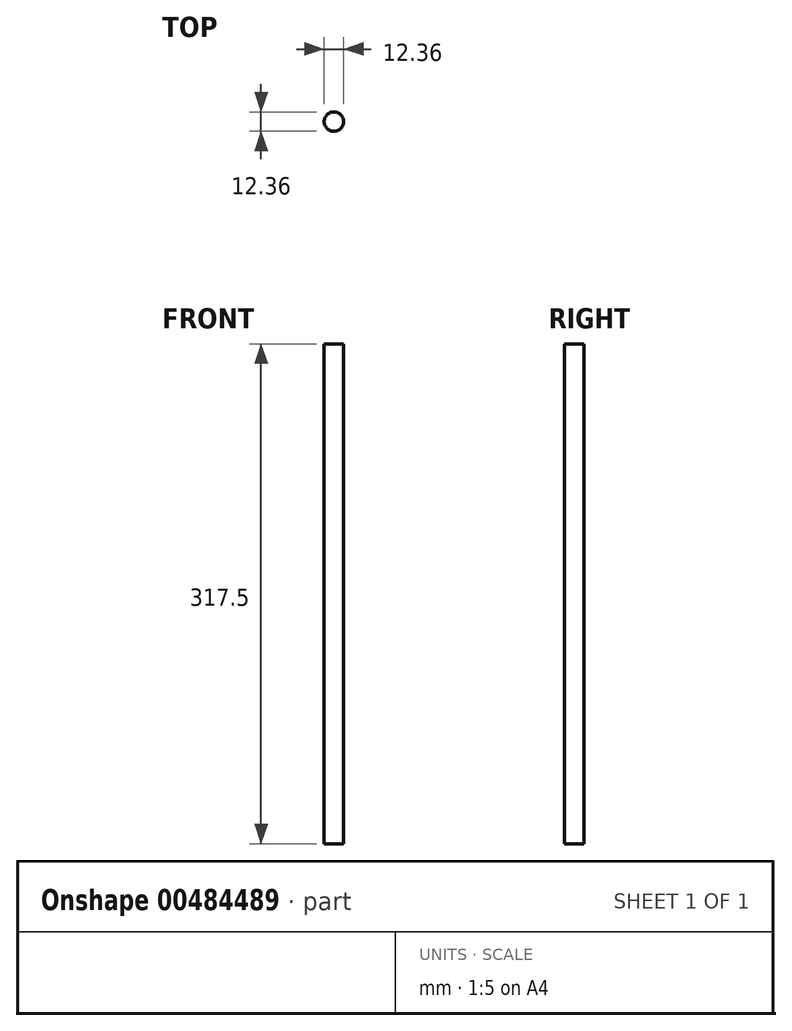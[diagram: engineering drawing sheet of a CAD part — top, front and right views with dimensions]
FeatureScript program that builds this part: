
annotation { "Feature Type Name" : "Feature", "Feature Type Description" : "" }
export const myFeature = defineFeature(function(context is Context, id is Id, definition is map)
    precondition{}
    {
        {
            var Q0;
            Q0=qCreatedBy(makeId("Top.planeOp"),FACE);
            var sketch = newSketch(context, id + "F0", { "sketchPlane" : qUnion([Q0])});
            skCircle(sketch, "E0", {"center": v(0, 0) * mm, "radius": 6.18 * mm});
            skSolve(sketch);
        }
        {
            var Q0;
            Q0 = qSketchRegion(id + "F0", true);
            extrude(context, id + "F1", {"entities" : qUnion([Q0]), "depth" : 317.5 * mm});
        }
    });
